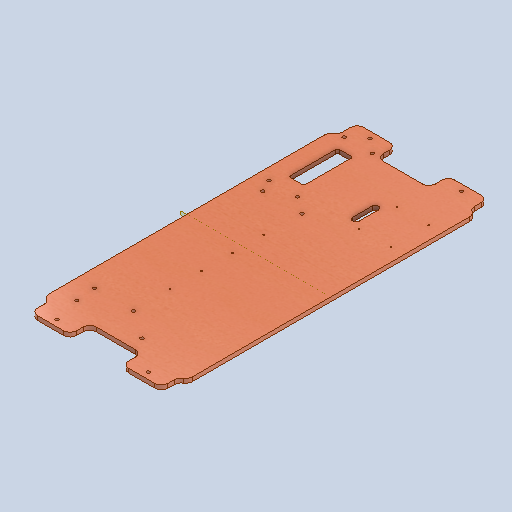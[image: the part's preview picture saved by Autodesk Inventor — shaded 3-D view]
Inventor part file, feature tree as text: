
AUTODESK INVENTOR PART (.ipt)
format: ipt  version: 2025.1 (Build 291241020, 241B)  size: 467,456 bytes
history: native  units: mm
features: sketch x10, reference x7, hole x6, other x6, extrude x4, plane x2, mirror x2, fillet x2, pattern_linear x1
ambient origin geometry x8: Origin, YZ Plane, XZ Plane, XY Plane, X Axis, Y Axis, Z Axis, Center Point
bodies: Solid1 (feature_tree)
feature tree (40):
  extrude  "Extrusion1"  Depth=220.0mm
  extrude  "Extrusion2"  Depth=5.0mm TaperAngle=0.0deg
  hole  "Hole1"  [1 undecoded]
  plane  "Work Plane1"
  plane  "Work Plane2"
  mirror  "Mirror1"
  mirror  "Mirror2"
  fillet  "Fillet1"  Radius=87.5mm
  hole  "Hole2"  [1 undecoded]
  pattern_linear  "Rectangular Pattern1"  Count1=5  [1 undecoded]
  hole  "Hole3"  [1 undecoded]
  hole  "Hole4"  [1 undecoded]
  hole  "Hole6"  [1 undecoded]
  hole  "Hole7"  [1 undecoded]
  extrude  "Extrusion4"  Depth=10.0mm
  fillet  "Fillet2"  Radius=48.0mm
  extrude  "Extrusion5"  Depth=10.0mm
  sketch  "Sketch1"  dims[d0=440.0mm d1=220.0mm]
  sketch  "Sketch2"  dims[d2=6.35mm d3=0.0mm d6=5.0mm d7=0.0mm]
  sketch  "Sketch3"  dims[d8=10.0mm]
  sketch  "Sketch4"  dims[d10=5.0mm d11=6.0mm d12=4.0mm d13=2.0mm d14=90.0deg d15=8.0mm d16=20.594885mm d17=10.0mm d18=87.5mm]
  sketch  "Sketch6"  dims[d19=132.075mm]
  sketch  "Sketch7"  dims[d20=5.0mm d21=6.0mm d22=4.0mm d23=2.0mm d24=90.0deg d25=8.0mm d26=20.594885mm d29=20.0mm d31=258.115mm d32=20.0mm d34=60.0mm]
  sketch  "Sketch9"  dims[d35=58.0mm]
  reference  "Reference4"
  reference  "Reference5"
  reference  "Reference6"
  sketch  "Sketch10"  dims[d36=49.0mm d37=50.0mm]
  reference  "Reference7"
  reference  "Reference8"
  reference  "Reference9"
  reference  "Reference10"
  sketch  "Sketch11"  dims[d38=20.0mm]
  sketch  "Sketch12"  dims[d39=2.1mm d40=6.0mm d41=4.0mm d42=2.0mm d43=90.0deg d44=6.0mm d45=0.0mm d46=100.0mm d49=5.0mm d50=6.0mm d51=10.0mm d52=2.5mm d53=90.0deg d54=8.0mm d55=20.594885mm d56=20.0mm d57=30.0mm d67=48.0mm d68=48.0mm d69=48.0mm d70=244.475mm d71=98.2375mm d72=20.0mm d73=2.6mm d74=6.0mm d75=4.0mm d76=2.0mm d77=90.0deg d78=10.0mm d79=0.0mm d80=30.0mm d81=60.0mm d82=10.0mm d83=30.0mm d84=5.0mm d85=6.0mm d86=4.0mm d87=2.0mm d88=90.0deg d89=8.0mm d90=20.594885mm d91=20.0mm d92=20.0mm d93=10.0mm d94=10.0mm d95=10.0mm d96=0.0mm d97=2.5mm d98=5.0mm d99=30.0mm d100=10.0mm d101=10.0mm d102=10.0mm d103=0.0mm]
  other  "MagDrop4.iam"
  other  "Connect4_LEG:1"
  other  "Connect4_LEG:2"
  other  "Connect4_RACK:1"
  other  "Control_Panel:1"
  other  "Control_Mount:1"
note: 7 required parameter values undecoded (feature->parameter linkage not recoverable at this tier; creation-order binding heuristic only, values carry confidence <= 0.55)
